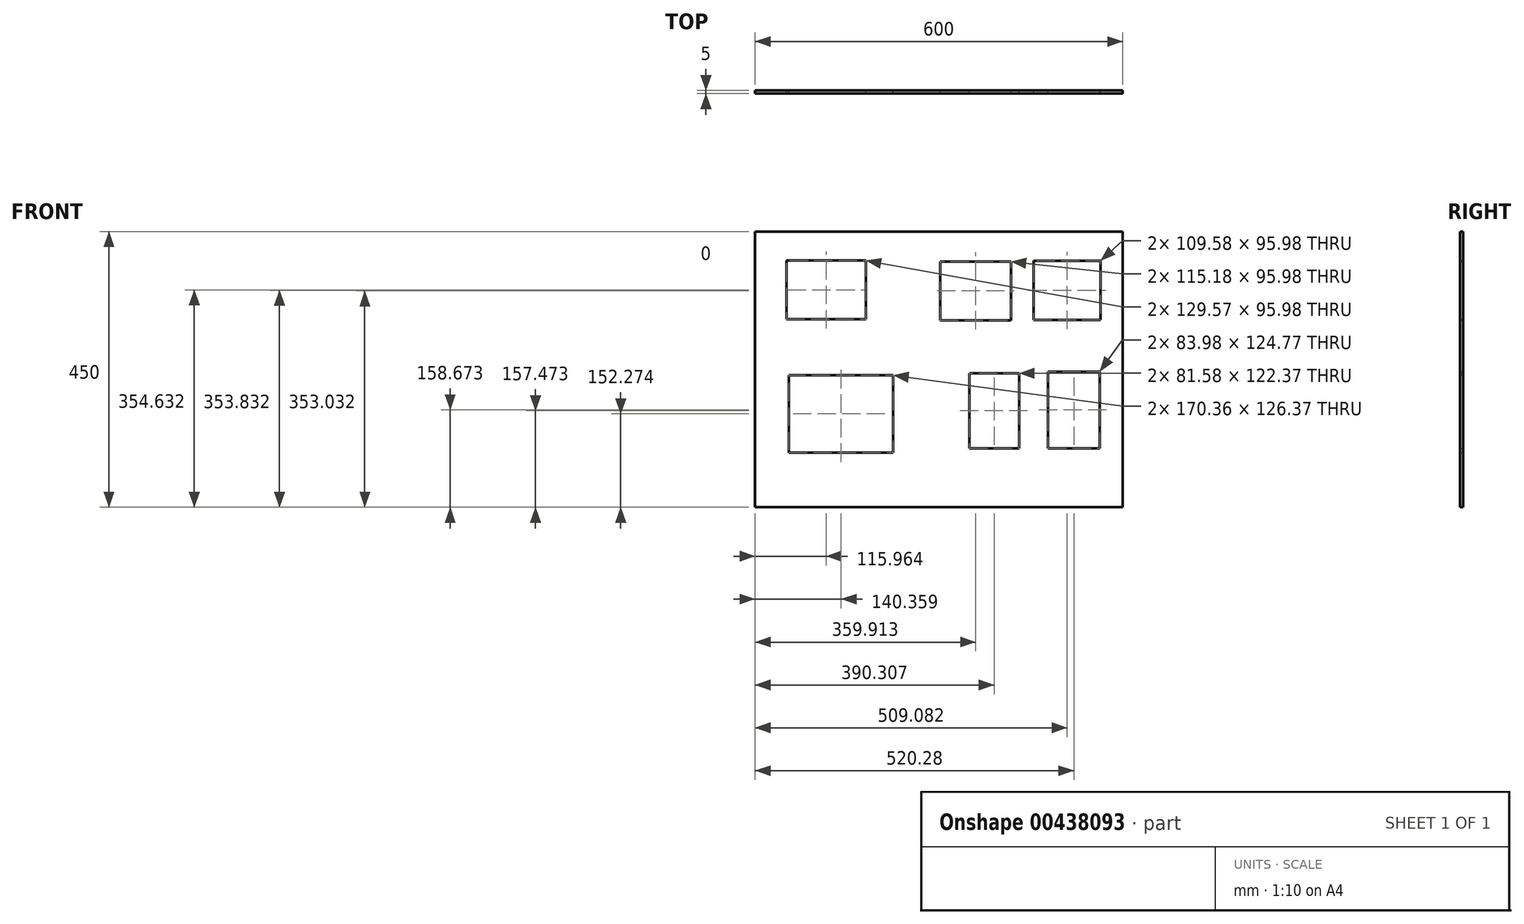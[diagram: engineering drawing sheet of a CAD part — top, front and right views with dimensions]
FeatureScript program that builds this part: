
annotation { "Feature Type Name" : "Feature", "Feature Type Description" : "" }
export const myFeature = defineFeature(function(context is Context, id is Id, definition is map)
    precondition{}
    {
        {
            var Q0;
            Q0=qCreatedBy(makeId("Front.planeOp"),FACE);
            var sketch = newSketch(context, id + "F0", { "sketchPlane" : qUnion([Q0])});
            skLineSegment(sketch, "E0.bottom", {"start": v(-237.94, 334.58) * mm, "end": v(362.06, 334.58) * mm});
            skLineSegment(sketch, "E0.top", {"start": v(-237.94, -115.42) * mm, "end": v(362.06, -115.42) * mm});
            skLineSegment(sketch, "E0.left", {"start": v(-237.94, 334.58) * mm, "end": v(-237.94, -115.42) * mm});
            skLineSegment(sketch, "E0.right", {"start": v(362.06, 334.58) * mm, "end": v(362.06, -115.42) * mm});
            skLineSegment(sketch, "E1", {"start": v(-237.94, 87.1) * mm, "end": v(-237.94, 127.1) * mm});
            skLineSegment(sketch, "E2", {"start": v(362.06, 127.1) * mm, "end": v(362.06, 109.58) * mm});
            skLineSegment(sketch, "E3", {"start": v(362.06, 109.58) * mm, "end": v(362.06, 87.1) * mm});
            skLineSegment(sketch, "E4", {"start": v(62.06, -115.42) * mm, "end": v(62.06, -65.42) * mm, "construction": true});
            skLineSegment(sketch, "E5", {"start": v(62.06, -65.42) * mm, "end": v(-237.94, -65.42) * mm, "construction": true});
            skLineSegment(sketch, "E6", {"start": v(-237.94, -65.42) * mm, "end": v(362.06, -65.42) * mm, "construction": true});
            skLineSegment(sketch, "E7", {"start": v(362.06, -65.42) * mm, "end": v(62.06, -65.42) * mm, "construction": true});
            skLineSegment(sketch, "E8", {"start": v(40.27, -65.42) * mm, "end": v(40.27, 114.58) * mm, "construction": true});
            skLineSegment(sketch, "E9.bottom", {"start": v(-182.76, 100.04) * mm, "end": v(-12.4, 100.04) * mm});
            skLineSegment(sketch, "E9.top", {"start": v(-182.76, -26.33) * mm, "end": v(-12.4, -26.33) * mm});
            skLineSegment(sketch, "E9.left", {"start": v(-182.76, 100.04) * mm, "end": v(-182.76, -26.33) * mm});
            skLineSegment(sketch, "E9.right", {"start": v(-12.4, 100.04) * mm, "end": v(-12.4, -26.33) * mm});
            skLineSegment(sketch, "E10.bottom", {"start": v(111.58, 103.24) * mm, "end": v(193.16, 103.24) * mm});
            skLineSegment(sketch, "E10.top", {"start": v(111.58, -19.13) * mm, "end": v(193.16, -19.13) * mm});
            skLineSegment(sketch, "E10.left", {"start": v(111.58, 103.24) * mm, "end": v(111.58, -19.13) * mm});
            skLineSegment(sketch, "E10.right", {"start": v(193.16, 103.24) * mm, "end": v(193.16, -19.13) * mm});
            skLineSegment(sketch, "E11.bottom", {"start": v(240.35, 105.64) * mm, "end": v(324.33, 105.64) * mm});
            skLineSegment(sketch, "E11.top", {"start": v(240.35, -19.13) * mm, "end": v(324.33, -19.13) * mm});
            skLineSegment(sketch, "E11.left", {"start": v(240.35, 105.64) * mm, "end": v(240.35, -19.13) * mm});
            skLineSegment(sketch, "E11.right", {"start": v(324.33, 105.64) * mm, "end": v(324.33, -19.13) * mm});
            skLineSegment(sketch, "E12.bottom", {"start": v(-186.76, 287.2) * mm, "end": v(-57.19, 287.2) * mm});
            skLineSegment(sketch, "E12.top", {"start": v(-186.76, 191.22) * mm, "end": v(-57.19, 191.22) * mm});
            skLineSegment(sketch, "E12.left", {"start": v(-186.76, 287.2) * mm, "end": v(-186.76, 191.22) * mm});
            skLineSegment(sketch, "E12.right", {"start": v(-57.19, 287.2) * mm, "end": v(-57.19, 191.22) * mm});
            skLineSegment(sketch, "E13.bottom", {"start": v(64.38, 285.6) * mm, "end": v(179.56, 285.6) * mm});
            skLineSegment(sketch, "E13.top", {"start": v(64.38, 189.62) * mm, "end": v(179.56, 189.62) * mm});
            skLineSegment(sketch, "E13.left", {"start": v(64.38, 285.6) * mm, "end": v(64.38, 189.62) * mm});
            skLineSegment(sketch, "E13.right", {"start": v(179.56, 285.6) * mm, "end": v(179.56, 189.62) * mm});
            skLineSegment(sketch, "E14.bottom", {"start": v(216.35, 286.4) * mm, "end": v(325.93, 286.4) * mm});
            skLineSegment(sketch, "E14.top", {"start": v(216.35, 190.42) * mm, "end": v(325.93, 190.42) * mm});
            skLineSegment(sketch, "E14.left", {"start": v(216.35, 286.4) * mm, "end": v(216.35, 190.42) * mm});
            skLineSegment(sketch, "E14.right", {"start": v(325.93, 286.4) * mm, "end": v(325.93, 190.42) * mm});
            skSolve(sketch);
        }
        {
            var Q0;
            {var subQ3=sQuery(id+"F0.wireOp",EDGE,"E0.bottom");Q0=makeQuery(id+"F0.imprint","IMPRINT",FACE,{"disambiguationData":[TD([[makeQuery(id+"F0.imprint","IMPRINT",EDGE,{"derivedFrom":subQ3}),-1.0]])]});}
            extrude(context, id + "F1", {"entities" : qUnion([Q0]), "depth" : 5 * mm});
        }
        {
            var Q0;
            {var subQ3=sQuery(id+"F0.wireOp",EDGE,"E0.bottom");Q0=makeQuery(id+"F0.imprint","IMPRINT",FACE,{"disambiguationData":[TD([[makeQuery(id+"F0.imprint","IMPRINT",EDGE,{"derivedFrom":subQ3}),-1.0]])]});}
            extrude(context, id + "F2", {"entities" : qUnion([Q0]), "depth" : 5 * mm});
        }
    });
